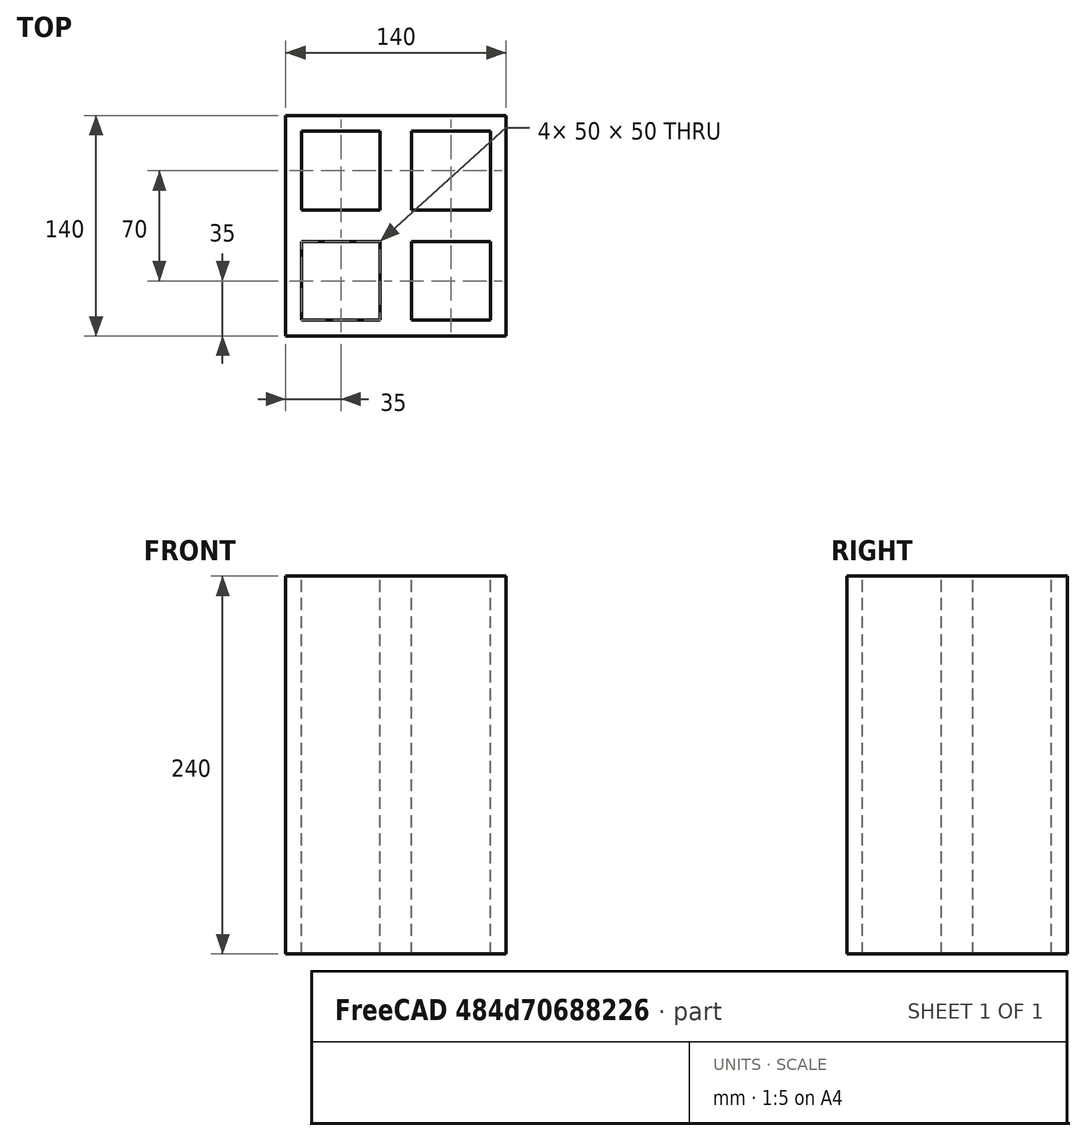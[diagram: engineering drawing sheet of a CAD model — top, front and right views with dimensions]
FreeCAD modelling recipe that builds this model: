
FCSTD DOCUMENT  (FreeCAD 0.21R33771 (Git))
Label: OJT1_T19R01_totxo
License: All rights reserved
LicenseURL: http://en.wikipedia.org/wiki/All_rights_reserved
objects: Sketcher::SketchObject×1, PartDesign::Pad×1, PartDesign::Body×1
note: 4 computed .brp shape members not serialized (recipe doc carries the construction recipe); baked Part::Feature solids carry a one-line shape summary decoded from their .brp

FEATURE [Sketcher::SketchObject] Sketch
  FullyConstrained = true
  MapMode = 5
  Support = -> [XY_Plane]
  sketch-geometry (20):
    g0: LineSegment StartX=-70 StartY=70 StartZ=0 EndX=70 EndY=70 EndZ=0
    g1: LineSegment StartX=70 StartY=70 StartZ=0 EndX=70 EndY=-70 EndZ=0
    g2: LineSegment StartX=70 StartY=-70 StartZ=0 EndX=-70 EndY=-70 EndZ=0
    g3: LineSegment StartX=-70 StartY=-70 StartZ=0 EndX=-70 EndY=70 EndZ=0
    g4: LineSegment StartX=-60 StartY=60 StartZ=0 EndX=-10 EndY=60 EndZ=0
    g5: LineSegment StartX=-10 StartY=60 StartZ=0 EndX=-10 EndY=10 EndZ=0
    g6: LineSegment StartX=-10 StartY=10 StartZ=0 EndX=-60 EndY=10 EndZ=0
    g7: LineSegment StartX=-60 StartY=10 StartZ=0 EndX=-60 EndY=60 EndZ=0
    g8: LineSegment StartX=-60 StartY=-10 StartZ=0 EndX=-10 EndY=-10 EndZ=0
    g9: LineSegment StartX=-10 StartY=-10 StartZ=0 EndX=-10 EndY=-60 EndZ=0
    g10: LineSegment StartX=-10 StartY=-60 StartZ=0 EndX=-60 EndY=-60 EndZ=0
    g11: LineSegment StartX=-60 StartY=-60 StartZ=0 EndX=-60 EndY=-10 EndZ=0
    g12: LineSegment StartX=10 StartY=60 StartZ=0 EndX=60 EndY=60 EndZ=0
    g13: LineSegment StartX=60 StartY=60 StartZ=0 EndX=60 EndY=10 EndZ=0
    g14: LineSegment StartX=60 StartY=10 StartZ=0 EndX=10 EndY=10 EndZ=0
    g15: LineSegment StartX=10 StartY=10 StartZ=0 EndX=10 EndY=60 EndZ=0
    g16: LineSegment StartX=10 StartY=-10 StartZ=0 EndX=60 EndY=-10 EndZ=0
    g17: LineSegment StartX=60 StartY=-10 StartZ=0 EndX=60 EndY=-60 EndZ=0
    g18: LineSegment StartX=60 StartY=-60 StartZ=0 EndX=10 EndY=-60 EndZ=0
    g19: LineSegment StartX=10 StartY=-60 StartZ=0 EndX=10 EndY=-10 EndZ=0
  constraints (56):
    c: Coincident(g0,g1)
    c: Coincident(g1,g2)
    c: Coincident(g2,g3)
    c: Coincident(g3,g0)
    c: Horizontal(g0)
    c: Horizontal(g2)
    c: Vertical(g1)
    c: Vertical(g3)
    c: Coincident(g4,g5)
    c: Coincident(g5,g6)
    c: Coincident(g6,g7)
    c: Coincident(g7,g4)
    c: Horizontal(g4)
    c: Horizontal(g6)
    c: Vertical(g5)
    c: Vertical(g7)
    c: Coincident(g8,g9)
    c: Coincident(g9,g10)
    c: Coincident(g10,g11)
    c: Coincident(g11,g8)
    c: Horizontal(g8)
    c: Horizontal(g10)
    c: Vertical(g9)
    c: Vertical(g11)
    c: Coincident(g12,g13)
    c: Coincident(g13,g14)
    c: Coincident(g14,g15)
    c: Coincident(g15,g12)
    c: Horizontal(g12)
    c: Horizontal(g14)
    c: Vertical(g13)
    c: Coincident(g16,g17)
    c: Coincident(g17,g18)
    c: Coincident(g18,g19)
    c: Coincident(g19,g16)
    c: Horizontal(g16)
    c: Horizontal(g18)
    c: Vertical(g17)
    c: Vertical(g19)
    c: Symmetric(g4,g12,g-2)
    c: Symmetric(g8,g16,g-2)
    c: Symmetric(g5,g8,g-1)
    c: Symmetric(g14,g16,g-1)
    c: DistanceX(g0,g4) = 10
    c: DistanceY(g4,g0) = 10
    c: DistanceX(g4,g4) = 50
    c: Equal(g4,g12)
    c: Equal(g12,g16)
    c: Equal(g16,g8)
    c: DistanceY(g6,g4) = 50
    c: DistanceX(g0,g0) = 140
    c: Equal(g0,g3)
    c: Equal(g7,g11)
    c: Equal(g15,g19)
    c: DistanceY(g2,g10) = 10
    c: DistanceX(g2,g10) = 10
FEATURE [PartDesign::Pad] Pad
  Direction = (0,0,1)
  Length = 240
  Length2 = 10
  Profile = -> Sketch
  ReferenceAxis = -> Sketch [N_Axis]
  Type = 0
FEATURE [PartDesign::Body] Body  label="totxo"
  Group = -> [Sketch,Pad]
  Origin = -> Origin
  Tip = -> Pad
